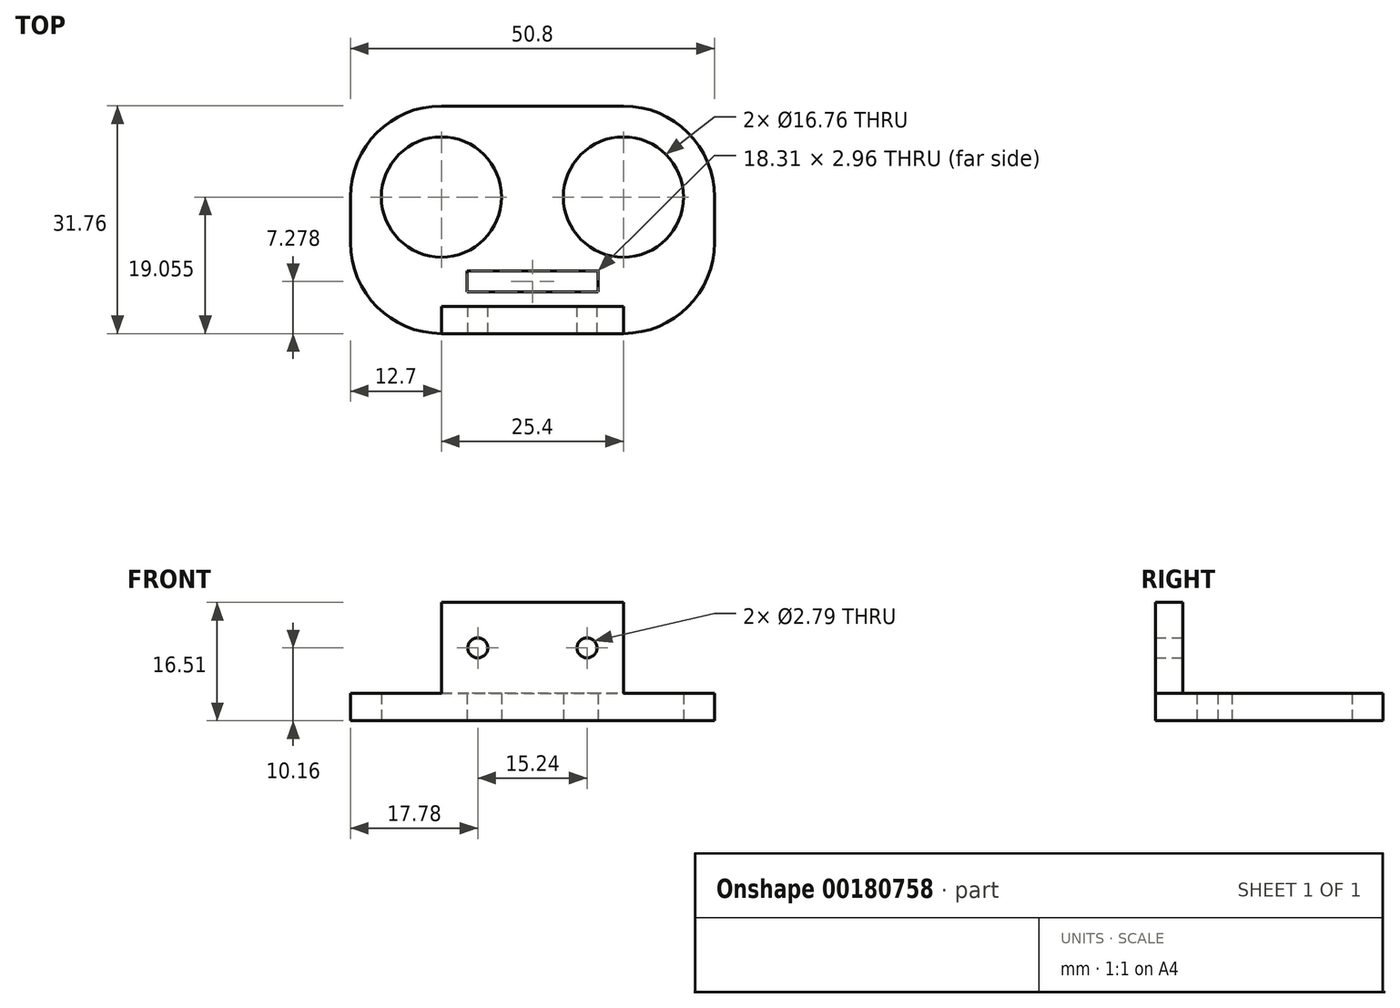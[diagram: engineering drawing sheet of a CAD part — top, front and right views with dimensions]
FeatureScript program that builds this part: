
annotation { "Feature Type Name" : "Feature", "Feature Type Description" : "" }
export const myFeature = defineFeature(function(context is Context, id is Id, definition is map)
    precondition{}
    {
        {
            var Q0;
            Q0=qCreatedBy(makeId("Top.planeOp"),FACE);
            var sketch = newSketch(context, id + "F0", { "sketchPlane" : qUnion([Q0])});
            skLineSegment(sketch, "E0.bottom", {"start": v(12.7, 15.87) * mm, "end": v(-12.7, 15.87) * mm});
            skLineSegment(sketch, "E0.top", {"start": v(12.7, -15.88) * mm, "end": v(-12.7, -15.88) * mm});
            skLineSegment(sketch, "E0.left", {"start": v(25.4, 3.17) * mm, "end": v(25.4, -3.17) * mm});
            skLineSegment(sketch, "E0.right", {"start": v(-25.4, 3.17) * mm, "end": v(-25.4, -3.17) * mm});
            skPoint(sketch, "E0.middle", {"position": v(0, 0) * mm});
            skLineSegment(sketch, "E1", {"start": v(-25.4, 3.18) * mm, "end": v(25.4, 3.18) * mm, "construction": true});
            skCircle(sketch, "E2", {"center": v(-12.7, 3.18) * mm, "radius": 8.38 * mm});
            skCircle(sketch, "E3", {"center": v(12.7, 3.18) * mm, "radius": 8.38 * mm});
            skPoint(sketch, "E4.visualSharp", {"position": v(-25.4, 15.87) * mm});
            skArc(sketch, "E4.filletArc", {"start": v(-12.7, 15.87) * mm, "mid": v(-21.68, 12.16) * mm, "end": v(-25.4, 3.17) * mm});
            skPoint(sketch, "E5.visualSharp", {"position": v(25.4, 15.87) * mm});
            skArc(sketch, "E5.filletArc", {"start": v(25.4, 3.17) * mm, "mid": v(21.68, 12.16) * mm, "end": v(12.7, 15.87) * mm});
            skPoint(sketch, "E6.visualSharp", {"position": v(25.4, -15.88) * mm});
            skArc(sketch, "E6.filletArc", {"start": v(12.7, -15.88) * mm, "mid": v(21.68, -12.16) * mm, "end": v(25.4, -3.18) * mm});
            skPoint(sketch, "E7.visualSharp", {"position": v(-25.4, -15.88) * mm});
            skArc(sketch, "E7.filletArc", {"start": v(-25.4, -3.18) * mm, "mid": v(-21.68, -12.16) * mm, "end": v(-12.7, -15.88) * mm});
            skSolve(sketch);
        }
        {
            var Q0;
            Q0=makeQuery(id+"F0.imprint","IMPRINT",FACE,{"disambiguationData":[TD([[makeQuery(id+"F0.imprint","IMPRINT",EDGE,{"derivedFrom":sQuery(id+"F0.wireOp",EDGE,"E0.bottom")}),1.0]])]});
            extrude(context, id + "F1", {"entities" : qUnion([Q0]), "depth" : 3.8 * mm});
        }
        {
            var Q0;
            Q0=makeQuery(id+"F1.opExtrude","CAP_FACE",FACE,{"disambiguationData":[OSD([sQuery(id+"F0.wireOp",EDGE,"E0.bottom"),sQuery(id+"F0.wireOp",EDGE,"E0.top"),sQuery(id+"F0.wireOp",EDGE,"E0.left"),sQuery(id+"F0.wireOp",EDGE,"E0.right"),sQuery(id+"F0.wireOp",EDGE,"E2"),sQuery(id+"F0.wireOp",EDGE,"E3"),sQuery(id+"F0.wireOp",EDGE,"E4.filletArc"),sQuery(id+"F0.wireOp",EDGE,"E5.filletArc"),sQuery(id+"F0.wireOp",EDGE,"E6.filletArc"),sQuery(id+"F0.wireOp",EDGE,"E7.filletArc")])],"isStart":false});
            var sketch = newSketch(context, id + "F2", { "sketchPlane" : qUnion([Q0])});
            skLineSegment(sketch, "E8", {"start": v(0, 15.88) * mm, "end": v(0, -15.88) * mm, "construction": true});
            skLineSegment(sketch, "E9.bottom", {"start": v(-12.7, -15.88) * mm, "end": v(12.7, -15.88) * mm});
            skLineSegment(sketch, "E9.top", {"start": v(-12.7, -12.06) * mm, "end": v(12.7, -12.06) * mm});
            skLineSegment(sketch, "E9.left", {"start": v(-12.7, -15.88) * mm, "end": v(-12.7, -12.06) * mm});
            skLineSegment(sketch, "E9.right", {"start": v(12.7, -15.88) * mm, "end": v(12.7, -12.06) * mm});
            skSolve(sketch);
        }
        {
            var Q0;
            Q0=makeQuery(id+"F2.imprint","IMPRINT",FACE,{"disambiguationData":[TD([[makeQuery(id+"F2.imprint","IMPRINT",EDGE,{"derivedFrom":sQuery(id+"F2.wireOp",EDGE,"E9.bottom")}),-1.0]])]});
            extrude(context, id + "F3", {"entities" : qUnion([Q0]), "operationType" : NewBodyOperationType.ADD, "depth" : 12.7 * mm});
        }
        {
            var Q0;
            Q0=makeQuery(id+"F3.opExtrude","SWEPT_FACE",FACE,{"disambiguationData":[OSD([sQuery(id+"F2.wireOp",EDGE,"E9.top")])]});
            var sketch = newSketch(context, id + "F4", { "sketchPlane" : qUnion([Q0])});
            skLineSegment(sketch, "E10", {"start": v(12.7, 10.16) * mm, "end": v(-12.7, 10.16) * mm, "construction": true});
            skLineSegment(sketch, "E11", {"start": v(-7.62, 3.81) * mm, "end": v(-7.62, 16.51) * mm, "construction": true});
            skLineSegment(sketch, "E12", {"start": v(7.62, 3.81) * mm, "end": v(7.62, 16.51) * mm, "construction": true});
            skCircle(sketch, "E13", {"center": v(7.62, 10.16) * mm, "radius": 1.4 * mm});
            skCircle(sketch, "E14", {"center": v(-7.62, 10.16) * mm, "radius": 1.4 * mm});
            skSolve(sketch);
        }
        {
            var Q0;
            Q0=makeQuery(id+"F4.imprint","IMPRINT",FACE,{"disambiguationData":[TD([[makeQuery(id+"F4.imprint","IMPRINT",EDGE,{"derivedFrom":sQuery(id+"F4.wireOp",EDGE,"E14")}),1.0]])]});
            var Q1;
            Q1=makeQuery(id+"F4.imprint","IMPRINT",FACE,{"disambiguationData":[TD([[makeQuery(id+"F4.imprint","IMPRINT",EDGE,{"derivedFrom":sQuery(id+"F4.wireOp",EDGE,"E13")}),1.0]])]});
            extrude(context, id + "F5", {"entities" : qUnion([Q0, Q1]), "operationType" : NewBodyOperationType.REMOVE, "oppositeDirection" : true, "depth" : 25.4 * mm});
        }
        {
            var Q0;
            Q0=makeQuery(id+"F1.opExtrude","CAP_FACE",FACE,{"disambiguationData":[OSD([sQuery(id+"F0.wireOp",EDGE,"E0.bottom"),sQuery(id+"F0.wireOp",EDGE,"E0.top"),sQuery(id+"F0.wireOp",EDGE,"E0.left"),sQuery(id+"F0.wireOp",EDGE,"E0.right"),sQuery(id+"F0.wireOp",EDGE,"E2"),sQuery(id+"F0.wireOp",EDGE,"E3"),sQuery(id+"F0.wireOp",EDGE,"E4.filletArc"),sQuery(id+"F0.wireOp",EDGE,"E5.filletArc"),sQuery(id+"F0.wireOp",EDGE,"E6.filletArc"),sQuery(id+"F0.wireOp",EDGE,"E7.filletArc")])],"isStart":true});
            var sketch = newSketch(context, id + "F6", { "sketchPlane" : qUnion([Q0])});
            skLineSegment(sketch, "E15.bottom", {"start": v(-9.16, 10.08) * mm, "end": v(9.16, 10.08) * mm});
            skLineSegment(sketch, "E15.top", {"start": v(-9.16, 7.12) * mm, "end": v(9.16, 7.12) * mm});
            skLineSegment(sketch, "E15.left", {"start": v(-9.16, 10.08) * mm, "end": v(-9.16, 7.12) * mm});
            skLineSegment(sketch, "E15.right", {"start": v(9.16, 10.08) * mm, "end": v(9.16, 7.12) * mm});
            skPoint(sketch, "E15.middle", {"position": v(0, 8.6) * mm});
            skCircle(sketch, "E16", {"center": v(0, 0) * mm, "radius": 2.13 * mm});
            skSolve(sketch);
        }
        {
            var Q0;
            Q0=makeQuery(id+"F6.imprint","IMPRINT",FACE,{"disambiguationData":[TD([[makeQuery(id+"F6.imprint","IMPRINT",EDGE,{"derivedFrom":sQuery(id+"F6.wireOp",EDGE,"E15.bottom")}),-1.0]])]});
            extrude(context, id + "F7", {"entities" : qUnion([Q0]), "operationType" : NewBodyOperationType.REMOVE, "oppositeDirection" : true, "depth" : 25.4 * mm});
        }
    });
